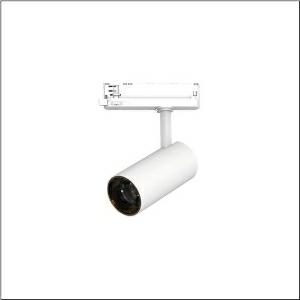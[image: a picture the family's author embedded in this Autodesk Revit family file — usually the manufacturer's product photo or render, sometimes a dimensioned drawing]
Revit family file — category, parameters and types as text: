
# Revit family: spot_31_slim_51sf127fa2b
name_source: partatom
category: Lighting Fixtures
units: mm (PartAtom-declared; Revit-internal decimal feet)

## family parameters
Cut with Voids When Loaded = No
Host = Face
Light Source = No
Part Type = Normal
Room Calculation Point = No
Round Connector Dimension = Use Diameter
Shared = No

## types (1)
- Spot 31 Slim (1 x LED, 2090 lm, 16.3 W, 2700K)
    Apparent Load = 16 VA
    CIE Flux Codes = 94 98 99 100 100
    Color Rendering = 90
    Color Temperature = 2700K
    Default Elevation = 1800 mm
    Description = Spot 31 Slim, directional spotlight, light control with reflector, of aluminium, LED rated luminous flux: 2.100lm, light colour: 927, control gear: ECG, with 3-phase adapter, mains connection: 220..240V, AC, 50/60Hz, housing, of aluminium, traffic white (RAL 9016), diameter: 70mm, adapter, of plastic, protection rating (complete): IP20, insulation class (complete): insulation class I (protective earthing), certification: CE, impact resistance: IK02, packaging unit: 1 piece
    Height = 210 mm
    Lamp = 1 x LED
    Lamp Light Flux = 2090 lm
    Lamp Power = 16.3 W
    Lamp count = 1
    Length = 70 mm
    Luminous efficacy = 128 lm/W
    Manufacturer = Siteco
    ModVariant = No
    Model = 51SF127FA2B
    Mounting Place = Ceiling
    Mounting Type = Pendant
    Number of Poles = 1
    OnlyDefault = Yes
    Power Factor = 1
    Product Name = Spot 31 Slim
    Product group = directional spotlight
    ProductGroupID = 905
    Protection Class = Protection class I
    Protection Degree = IP 20
    RLX_Detail_Level = 1
    RLX_Emergency_Light_Flux = 0 lm
    RLX_Emergency_Type = 0
    RLX_Emergency_Type_DB = No
    RlxData = <blob elided: 14169 chars, md5=1a2f4d1c>
    Socket = socket
    Standby Power = 0 W
    System Light Flux = 2090 lm
    System Power = 16 W
    Type Comments = Product without accessories
    Type Image = l_1228468.jpg
    URL = http://relux.com
    VarID = ---
    Voltage = 0 V
    Weight = 0.00 kg
    Width = 0 mm  [stored 0 ft]

note: [stored X ft] marks values corroborated as IEEE doubles in the binary element streams (Revit-internal decimal feet)

## geometry (parser evidence)
native form markers: Sweep x10
no freeform markers — native parametric forms only
